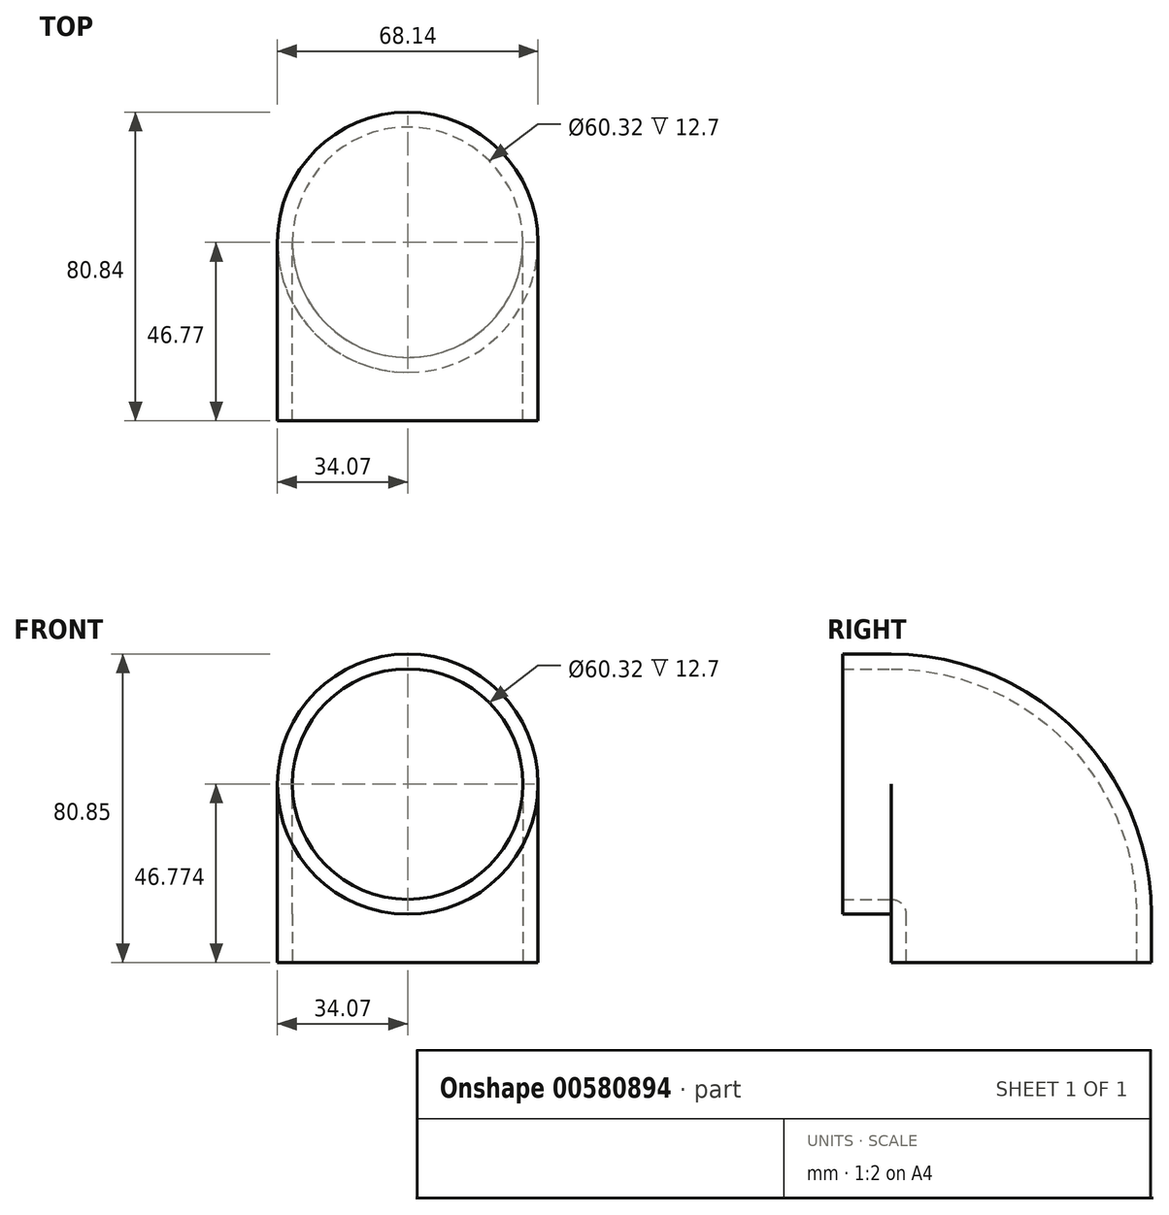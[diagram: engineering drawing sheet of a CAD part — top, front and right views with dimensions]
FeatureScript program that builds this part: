
annotation { "Feature Type Name" : "Feature", "Feature Type Description" : "" }
export const myFeature = defineFeature(function(context is Context, id is Id, definition is map)
    precondition{}
    {
        {
            var Q0;
            Q0=qCreatedBy(makeId("Top.planeOp"),FACE);
            var sketch = newSketch(context, id + "F0", { "sketchPlane" : qUnion([Q0])});
            skCircle(sketch, "E0", {"center": v(0, 0) * mm, "radius": 30.16 * mm});
            skCircle(sketch, "E1.0", {"center": v(0, 0) * mm, "radius": 34.07 * mm});
            skSolve(sketch);
        }
        {
            var Q0;
            Q0=makeQuery(id+"F0.imprint","IMPRINT",FACE,{"disambiguationData":[TD([[makeQuery(id+"F0.imprint","IMPRINT",EDGE,{"derivedFrom":sQuery(id+"F0.wireOp",EDGE,"E0")}),-1.0]])]});
            extrude(context, id + "F1", {"entities" : qUnion([Q0]), "depth" : 12.7 * mm, "offsetDistance" : 25 * mm});
        }
        {
            var Q0;
            Q0=makeQuery(id+"F1.opExtrude","CAP_FACE",FACE,{"disambiguationData":[OSD([sQuery(id+"F0.wireOp",EDGE,"E0"),sQuery(id+"F0.wireOp",EDGE,"E1.0")])],"isStart":false});
            var sketch = newSketch(context, id + "F2", { "sketchPlane" : qUnion([Q0])});
            skCircle(sketch, "E2.0", {"center": v(0, 0) * mm, "radius": 34.07 * mm});
            skCircle(sketch, "E3.0", {"center": v(0, 0) * mm, "radius": 30.16 * mm});
            skLineSegment(sketch, "E4", {"start": v(0, -34.07) * mm, "end": v(43.14, -34.07) * mm, "construction": true});
            skSolve(sketch);
        }
        {
            var Q0;
            Q0=makeQuery(id+"F2.imprint","IMPRINT",FACE,{"disambiguationData":[TD([[makeQuery(id+"F2.imprint","IMPRINT",EDGE,{"derivedFrom":sQuery(id+"F2.wireOp",EDGE,"E2.0")}),1.0]])]});
            var Q1;
            Q1=sQuery(id+"F2.wireOp",EDGE,"E4");
            revolve(context, id + "F3", {"operationType" : NewBodyOperationType.ADD, "entities" : qUnion([Q0]), "axis" : qUnion([Q1]), "revolveType" : RevolveType.ONE_DIRECTION, "angle" : 90 * degree});
        }
        {
            var Q0;
            Q0=makeQuery(id+"F3.opRevolve","CAP_FACE",FACE,{"disambiguationData":[OSD([sQuery(id+"F2.wireOp",EDGE,"E2.0"),sQuery(id+"F2.wireOp",EDGE,"E3.0")])],"isStart":false});
            extrude(context, id + "F4", {"entities" : qUnion([Q0]), "operationType" : NewBodyOperationType.ADD, "depth" : 12.7 * mm, "offsetDistance" : 25 * mm});
        }
    });
